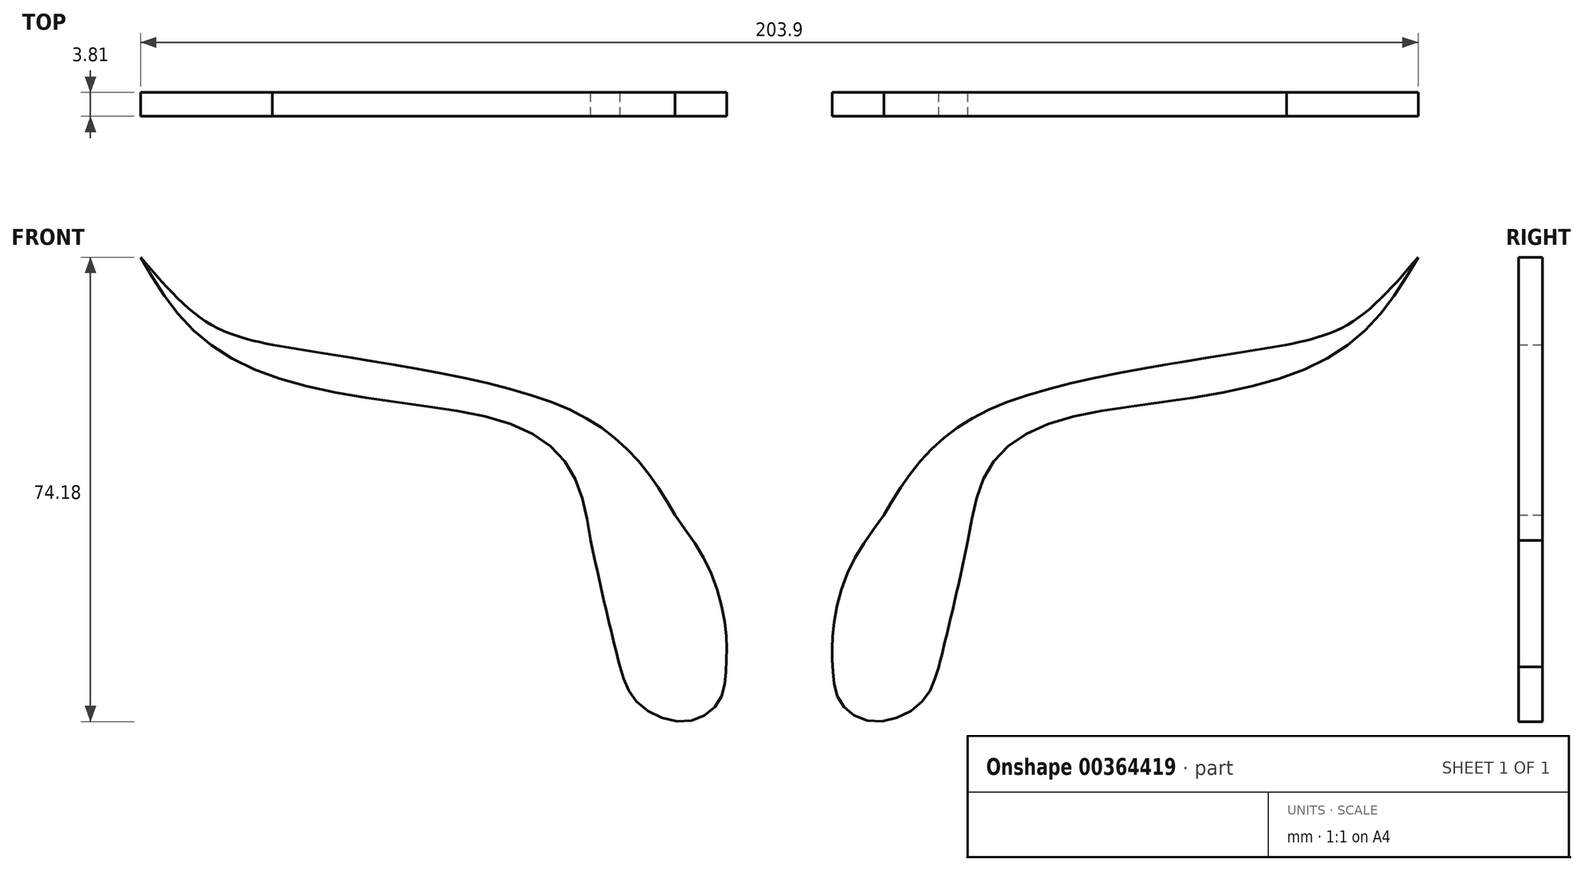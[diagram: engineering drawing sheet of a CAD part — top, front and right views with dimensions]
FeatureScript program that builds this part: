
annotation { "Feature Type Name" : "Feature", "Feature Type Description" : "" }
export const myFeature = defineFeature(function(context is Context, id is Id, definition is map)
    precondition{}
    {
        {
            var Q0;
            Q0=qCreatedBy(makeId("Front.planeOp"),FACE);
            var sketch = newSketch(context, id + "F0", { "sketchPlane" : qUnion([Q0])});
            skPoint(sketch, "E0", {"position": v(-101.95, 50.52) * mm});
            skPoint(sketch, "E1", {"position": v(-94.65, 40) * mm});
            skPoint(sketch, "E2", {"position": v(-82.67, 32.12) * mm});
            skPoint(sketch, "E3", {"position": v(-61.65, 27.45) * mm});
            skPoint(sketch, "E4", {"position": v(-41.5, 23.36) * mm});
            skPoint(sketch, "E5", {"position": v(-33.03, 16.06) * mm});
            skPoint(sketch, "E6", {"position": v(-30.11, 5.26) * mm});
            skPoint(sketch, "E7", {"position": v(-27.78, -5.26) * mm});
            skPoint(sketch, "E8", {"position": v(-25.44, -14.9) * mm});
            skPoint(sketch, "E9", {"position": v(-15.22, -23.65) * mm});
            skPoint(sketch, "E10", {"position": v(-8.5, -14.9) * mm});
            skPoint(sketch, "E11", {"position": v(-8.5, -9.64) * mm});
            skPoint(sketch, "E12", {"position": v(-10.84, 0) * mm});
            skPoint(sketch, "E13", {"position": v(-16.68, 9.34) * mm});
            skPoint(sketch, "E14", {"position": v(-23.98, 19.56) * mm});
            skPoint(sketch, "E15", {"position": v(-36.54, 27.45) * mm});
            skPoint(sketch, "E16", {"position": v(-61.36, 33.29) * mm});
            skPoint(sketch, "E17", {"position": v(-80.92, 36.5) * mm});
            skFitSpline(sketch, "E18", {"points": [v(-101.95, 50.52) * mm, v(-94.65, 40) * mm, v(-82.67, 32.12) * mm, v(-61.65, 27.45) * mm, v(-41.5, 23.36) * mm, v(-33.03, 16.06) * mm, v(-30.11, 5.26) * mm], "startDerivative": vector(42.5, -72) * mm, "endDerivative": vector(12.6, -79.7) * mm});
            skFitSpline(sketch, "E19", {"points": [v(-30.11, 5.26) * mm, v(-27.78, -5.26) * mm, v(-25.44, -14.9) * mm], "startDerivative": vector(4.53, -20.83) * mm, "endDerivative": vector(4.82, -19.45) * mm});
            skPoint(sketch, "E20", {"position": v(-22.81, -20.44) * mm});
            skPoint(sketch, "E21", {"position": v(-9.67, -20.44) * mm});
            skFitSpline(sketch, "E22", {"points": [v(-25.44, -14.9) * mm, v(-22.81, -20.44) * mm, v(-15.22, -23.65) * mm, v(-9.67, -20.44) * mm, v(-8.5, -14.9) * mm, v(-8.5, -9.64) * mm, v(-10.84, 0) * mm, v(-16.68, 9.34) * mm], "startDerivative": vector(13.42, -44.72) * mm, "endDerivative": vector(-37.7, 52.63) * mm});
            skFitSpline(sketch, "E23", {"points": [v(-16.68, 9.34) * mm, v(-23.98, 19.56) * mm, v(-36.54, 27.45) * mm, v(-61.36, 33.29) * mm, v(-80.92, 36.5) * mm], "startDerivative": vector(-27.63, 49.97) * mm, "endDerivative": vector(-69.74, 11.1) * mm});
            skPoint(sketch, "E24", {"position": v(-91.14, 40) * mm});
            skFitSpline(sketch, "E25", {"points": [v(-80.92, 36.5) * mm, v(-91.14, 40) * mm, v(-101.95, 50.52) * mm], "startDerivative": vector(-22.83, 4.95) * mm, "endDerivative": vector(-19.32, 22.6) * mm});
            skPoint(sketch, "E26.MirrorP", {"position": v(94.65, 40) * mm});
            skPoint(sketch, "E27.MirrorP", {"position": v(8.5, -14.9) * mm});
            skPoint(sketch, "E28.MirrorP", {"position": v(30.11, 5.26) * mm});
            skPoint(sketch, "E29.MirrorP", {"position": v(9.67, -20.44) * mm});
            skPoint(sketch, "E30.MirrorP", {"position": v(80.92, 36.5) * mm});
            skPoint(sketch, "E31.MirrorP", {"position": v(16.68, 9.34) * mm});
            skPoint(sketch, "E32.MirrorP", {"position": v(8.5, -9.64) * mm});
            skPoint(sketch, "E33.MirrorP", {"position": v(91.14, 40) * mm});
            skPoint(sketch, "E34.MirrorP", {"position": v(27.78, -5.26) * mm});
            skPoint(sketch, "E35.MirrorP", {"position": v(61.65, 27.45) * mm});
            skPoint(sketch, "E36.MirrorP", {"position": v(41.5, 23.36) * mm});
            skPoint(sketch, "E37.MirrorP", {"position": v(33.03, 16.06) * mm});
            skFitSpline(sketch, "E38.MirrorCS", {"points": [v(101.95, 50.52) * mm, v(94.65, 40) * mm, v(82.67, 32.12) * mm, v(61.65, 27.45) * mm, v(41.5, 23.36) * mm, v(33.03, 16.06) * mm, v(30.11, 5.26) * mm], "startDerivative": vector(-42.5, -72) * mm, "endDerivative": vector(-12.6, -79.7) * mm});
            skFitSpline(sketch, "E39.MirrorCS", {"points": [v(30.11, 5.26) * mm, v(27.78, -5.26) * mm, v(25.44, -14.9) * mm], "startDerivative": vector(-4.53, -20.83) * mm, "endDerivative": vector(-4.82, -19.45) * mm});
            skFitSpline(sketch, "E40.MirrorCS", {"points": [v(25.44, -14.9) * mm, v(22.81, -20.44) * mm, v(15.22, -23.65) * mm, v(9.67, -20.44) * mm, v(8.5, -14.9) * mm, v(8.5, -9.64) * mm, v(10.84, 0) * mm, v(16.68, 9.34) * mm], "startDerivative": vector(-13.42, -44.72) * mm, "endDerivative": vector(37.7, 52.63) * mm});
            skFitSpline(sketch, "E41.MirrorCS", {"points": [v(16.68, 9.34) * mm, v(23.98, 19.56) * mm, v(36.54, 27.45) * mm, v(61.36, 33.29) * mm, v(80.92, 36.5) * mm], "startDerivative": vector(27.63, 49.97) * mm, "endDerivative": vector(69.74, 11.1) * mm});
            skFitSpline(sketch, "E42.MirrorCS", {"points": [v(80.92, 36.5) * mm, v(91.14, 40) * mm, v(101.95, 50.52) * mm], "startDerivative": vector(22.83, 4.95) * mm, "endDerivative": vector(19.32, 22.6) * mm});
            skSolve(sketch);
        }
        {
            var Q0;
            Q0=qSketchRegion(id+"F0",true);
            extrude(context, id + "F1", {"entities" : qUnion([Q0]), "depth" : 3.8 * mm});
        }
    });
